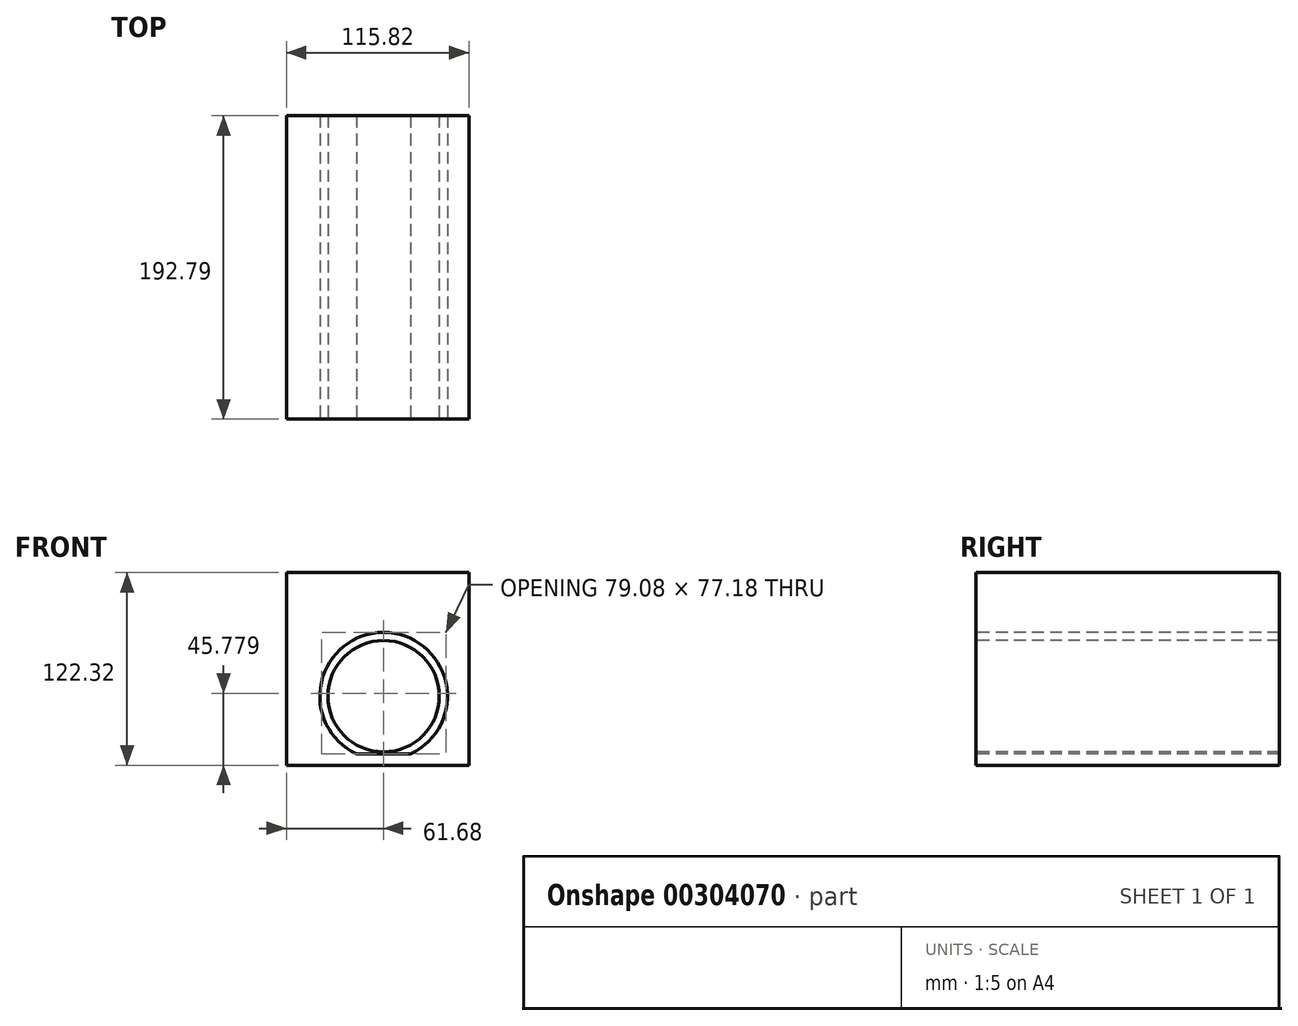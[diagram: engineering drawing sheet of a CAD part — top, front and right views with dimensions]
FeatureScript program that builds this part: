
annotation { "Feature Type Name" : "Feature", "Feature Type Description" : "" }
export const myFeature = defineFeature(function(context is Context, id is Id, definition is map)
    precondition{}
    {
        {
            var Q0;
            Q0=qCreatedBy(makeId("Front.planeOp"),FACE);
            var sketch = newSketch(context, id + "F0", { "sketchPlane" : qUnion([Q0])});
            skLineSegment(sketch, "E0.bottom", {"start": v(-61.68, 47.11) * mm, "end": v(54.14, 47.11) * mm});
            skLineSegment(sketch, "E0.top", {"start": v(-61.68, 24.16) * mm, "end": v(54.14, 24.16) * mm});
            skLineSegment(sketch, "E0.left", {"start": v(-61.68, 47.11) * mm, "end": v(-61.68, 24.16) * mm});
            skLineSegment(sketch, "E0.right", {"start": v(54.14, 47.11) * mm, "end": v(54.14, 24.16) * mm});
            skLineSegment(sketch, "E1.top", {"start": v(-61.68, -75.21) * mm, "end": v(54.14, -75.21) * mm});
            skLineSegment(sketch, "E1.left", {"start": v(-61.68, 24.16) * mm, "end": v(-61.68, -75.21) * mm});
            skLineSegment(sketch, "E1.right", {"start": v(54.14, 24.16) * mm, "end": v(54.14, -75.21) * mm});
            skLineSegment(sketch, "E2.bottom", {"start": v(-49, 9.08) * mm, "end": v(41.46, 9.08) * mm});
            skLineSegment(sketch, "E2.top", {"start": v(-49, -68.02) * mm, "end": v(41.46, -68.02) * mm});
            skLineSegment(sketch, "E2.left", {"start": v(-49, 9.08) * mm, "end": v(-49, -68.02) * mm});
            skLineSegment(sketch, "E2.right", {"start": v(41.46, 9.08) * mm, "end": v(41.46, -68.02) * mm});
            skCircle(sketch, "E3", {"center": v(0, -31.35) * mm, "radius": 35.38 * mm});
            skCircle(sketch, "E4", {"center": v(0, -31.35) * mm, "radius": 40.51 * mm});
            skCircle(sketch, "E5", {"center": v(0, -31.35) * mm, "radius": 10.17 * mm});
            skLineSegment(sketch, "E6", {"start": v(0, -31.35) * mm, "end": v(-29.89, -50.28) * mm});
            skLineSegment(sketch, "E7", {"start": v(-29.89, -50.28) * mm, "end": v(0, -34.44) * mm});
            skLineSegment(sketch, "E8", {"start": v(0, -34.44) * mm, "end": v(31.7, -47.05) * mm});
            skLineSegment(sketch, "E9", {"start": v(31.7, -47.05) * mm, "end": v(0, -31.35) * mm});
            skLineSegment(sketch, "E10", {"start": v(0, -34.44) * mm, "end": v(-11.1, 2.24) * mm});
            skLineSegment(sketch, "E11", {"start": v(-11.1, 2.24) * mm, "end": v(0, -27.59) * mm});
            skSolve(sketch);
        }
        {
            var Q0;
            Q0=makeQuery(id+"F0.imprint","IMPRINT",FACE,{"disambiguationData":[TD([[makeQuery(id+"F0.imprint","IMPRINT",EDGE,{"derivedFrom":sQuery(id+"F0.wireOp",EDGE,"E0.bottom")}),-1.0]])]});
            var Q1;
            Q1=makeQuery(id+"F0.imprint","IMPRINT",FACE,{"disambiguationData":[TD([[makeQuery(id+"F0.imprint","IMPRINT",EDGE,{"derivedFrom":sQuery(id+"F0.wireOp",EDGE,"E0.top")}),-1.0]])]});
            var Q2;
            {var subQ0=sQuery(id+"F0.wireOp",EDGE,"E2.left");Q2=makeQuery(id+"F0.imprint","IMPRINT",FACE,{"disambiguationData":[TD([[makeQuery(id+"F0.imprint","IMPRINT",EDGE,{"derivedFrom":subQ0}),1.0]])]});}
            var Q3;
            {var subQ0=sQuery(id+"F0.wireOp",EDGE,"E2.right");Q3=makeQuery(id+"F0.imprint","IMPRINT",FACE,{"disambiguationData":[TD([[makeQuery(id+"F0.imprint","IMPRINT",EDGE,{"derivedFrom":subQ0}),-1.0]])]});}
            var Q4;
            {var subQ0=sQuery(id+"F0.wireOp",EDGE,"E4");var subQ1=sQuery(id+"F0.wireOp",EDGE,"E2.top");var subQ2=makeQuery(id+"F0.imprint","INTERSECT",VERTEX,{"disambiguationData":[OD(0.0)],"derivedFrom":[subQ1,subQ0]});Q4=makeQuery(id+"F0.imprint","IMPRINT",FACE,{"disambiguationData":[TD([[makeQuery(id+"F0.imprint","IMPRINT",EDGE,{"disambiguationData":[TD([[subQ2,-1.0]])],"derivedFrom":subQ1}),-1.0]])]});}
            var Q5;
            {var subQ3=sQuery(id+"F0.wireOp",EDGE,"E5");var subQ7=makeQuery(id+"F0.imprint","INTERSECT",VERTEX,{"derivedFrom":[subQ3,sQuery(id+"F0.wireOp",EDGE,"E11")]});Q5=makeQuery(id+"F0.imprint","IMPRINT",FACE,{"disambiguationData":[TD([[makeQuery(id+"F0.imprint","IMPRINT",EDGE,{"disambiguationData":[TD([[subQ7,-1.0]])],"derivedFrom":subQ3}),1.0]])]});}
            var Q6;
            {var subQ0=sQuery(id+"F0.wireOp",EDGE,"E10");var subQ1=sQuery(id+"F0.wireOp",EDGE,"E5");var subQ2=makeQuery(id+"F0.imprint","INTERSECT",VERTEX,{"derivedFrom":[subQ1,subQ0]});Q6=makeQuery(id+"F0.imprint","IMPRINT",FACE,{"disambiguationData":[TD([[makeQuery(id+"F0.imprint","IMPRINT",EDGE,{"disambiguationData":[TD([[subQ2,-1.0]])],"derivedFrom":subQ1}),1.0]])]});}
            var Q7;
            {var subQ3=sQuery(id+"F0.wireOp",EDGE,"E10");var subQ5=sQuery(id+"F0.wireOp",EDGE,"E5");var subQ7=makeQuery(id+"F0.imprint","INTERSECT",VERTEX,{"derivedFrom":[subQ5,subQ3]});Q7=makeQuery(id+"F0.imprint","IMPRINT",FACE,{"disambiguationData":[TD([[makeQuery(id+"F0.imprint","IMPRINT",EDGE,{"disambiguationData":[TD([[subQ7,-1.0]])],"derivedFrom":subQ5}),-1.0]])]});}
            var Q8;
            {var subQ0=sQuery(id+"F0.wireOp",EDGE,"E7");var subQ5=sQuery(id+"F0.wireOp",EDGE,"E5");var subQ6=makeQuery(id+"F0.imprint","INTERSECT",VERTEX,{"derivedFrom":[subQ5,subQ0]});Q8=makeQuery(id+"F0.imprint","IMPRINT",FACE,{"disambiguationData":[TD([[makeQuery(id+"F0.imprint","IMPRINT",EDGE,{"disambiguationData":[TD([[subQ6,-1.0]])],"derivedFrom":subQ5}),-1.0]])]});}
            var Q9;
            {var subQ3=sQuery(id+"F0.wireOp",EDGE,"E11");var subQ5=sQuery(id+"F0.wireOp",EDGE,"E5");var subQ6=makeQuery(id+"F0.imprint","INTERSECT",VERTEX,{"derivedFrom":[subQ5,subQ3]});Q9=makeQuery(id+"F0.imprint","IMPRINT",FACE,{"disambiguationData":[TD([[makeQuery(id+"F0.imprint","IMPRINT",EDGE,{"disambiguationData":[TD([[subQ6,1.0]])],"derivedFrom":subQ5}),-1.0]])]});}
            var Q10;
            {var subQ4=sQuery(id+"F0.wireOp",EDGE,"E4");var subQ8=sQuery(id+"F0.wireOp",EDGE,"E2.bottom");var subQ9=makeQuery(id+"F0.imprint","INTERSECT",VERTEX,{"disambiguationData":[OD(0.0)],"derivedFrom":[subQ8,subQ4]});Q10=makeQuery(id+"F0.imprint","IMPRINT",FACE,{"disambiguationData":[TD([[makeQuery(id+"F0.imprint","IMPRINT",EDGE,{"disambiguationData":[TD([[subQ9,-1.0]])],"derivedFrom":subQ8}),-1.0]])]});}
            var Q11;
            {var subQ0=sQuery(id+"F0.wireOp",EDGE,"E6");var subQ1=sQuery(id+"F0.wireOp",EDGE,"E5");var subQ2=makeQuery(id+"F0.imprint","INTERSECT",VERTEX,{"derivedFrom":[subQ1,subQ0]});Q11=makeQuery(id+"F0.imprint","IMPRINT",FACE,{"disambiguationData":[TD([[makeQuery(id+"F0.imprint","IMPRINT",EDGE,{"disambiguationData":[TD([[subQ2,-1.0]])],"derivedFrom":subQ1}),1.0]])]});}
            var Q12;
            {var subQ0=sQuery(id+"F0.wireOp",EDGE,"E4");var subQ1=sQuery(id+"F0.wireOp",EDGE,"E2.bottom");var subQ2=makeQuery(id+"F0.imprint","INTERSECT",VERTEX,{"disambiguationData":[OD(0.0)],"derivedFrom":[subQ1,subQ0]});Q12=makeQuery(id+"F0.imprint","IMPRINT",FACE,{"disambiguationData":[TD([[makeQuery(id+"F0.imprint","IMPRINT",EDGE,{"disambiguationData":[TD([[subQ2,-1.0]])],"derivedFrom":subQ1}),1.0]])]});}
            var Q13;
            {var subQ1=sQuery(id+"F0.wireOp",EDGE,"E8");var subQ3=sQuery(id+"F0.wireOp",EDGE,"E5");var subQ4=makeQuery(id+"F0.imprint","INTERSECT",VERTEX,{"derivedFrom":[subQ3,subQ1]});Q13=makeQuery(id+"F0.imprint","IMPRINT",FACE,{"disambiguationData":[TD([[makeQuery(id+"F0.imprint","IMPRINT",EDGE,{"disambiguationData":[TD([[subQ4,-1.0]])],"derivedFrom":subQ3}),1.0]])]});}
            var Q14;
            {var subQ0=sQuery(id+"F0.wireOp",EDGE,"E11");var subQ1=sQuery(id+"F0.wireOp",EDGE,"E5");var subQ2=makeQuery(id+"F0.imprint","INTERSECT",VERTEX,{"derivedFrom":[subQ1,subQ0]});Q14=makeQuery(id+"F0.imprint","IMPRINT",FACE,{"disambiguationData":[TD([[makeQuery(id+"F0.imprint","IMPRINT",EDGE,{"disambiguationData":[TD([[subQ2,-1.0]])],"derivedFrom":subQ1}),-1.0]])]});}
            var Q15;
            {var subQ0=sQuery(id+"F0.wireOp",EDGE,"E6");var subQ1=sQuery(id+"F0.wireOp",EDGE,"E5");var subQ2=makeQuery(id+"F0.imprint","INTERSECT",VERTEX,{"derivedFrom":[subQ1,subQ0]});Q15=makeQuery(id+"F0.imprint","IMPRINT",FACE,{"disambiguationData":[TD([[makeQuery(id+"F0.imprint","IMPRINT",EDGE,{"disambiguationData":[TD([[subQ2,-1.0]])],"derivedFrom":subQ1}),-1.0]])]});}
            var Q16;
            {var subQ0=sQuery(id+"F0.wireOp",EDGE,"E7");var subQ1=sQuery(id+"F0.wireOp",EDGE,"E5");var subQ2=makeQuery(id+"F0.imprint","INTERSECT",VERTEX,{"derivedFrom":[subQ1,subQ0]});Q16=makeQuery(id+"F0.imprint","IMPRINT",FACE,{"disambiguationData":[TD([[makeQuery(id+"F0.imprint","IMPRINT",EDGE,{"disambiguationData":[TD([[subQ2,-1.0]])],"derivedFrom":subQ1}),1.0]])]});}
            var Q17;
            {var subQ0=sQuery(id+"F0.wireOp",EDGE,"E8");var subQ1=sQuery(id+"F0.wireOp",EDGE,"E5");var subQ2=makeQuery(id+"F0.imprint","INTERSECT",VERTEX,{"derivedFrom":[subQ1,subQ0]});Q17=makeQuery(id+"F0.imprint","IMPRINT",FACE,{"disambiguationData":[TD([[makeQuery(id+"F0.imprint","IMPRINT",EDGE,{"disambiguationData":[TD([[subQ2,-1.0]])],"derivedFrom":subQ1}),-1.0]])]});}
            extrude(context, id + "F1", {"entities" : qUnion([Q0, Q1, Q2, Q3, Q4, Q5, Q6, Q7, Q8, Q9, Q10, Q11, Q12, Q13, Q14, Q15, Q16, Q17]), "oppositeDirection" : true, "depth" : 192.79 * mm});
        }
    });
